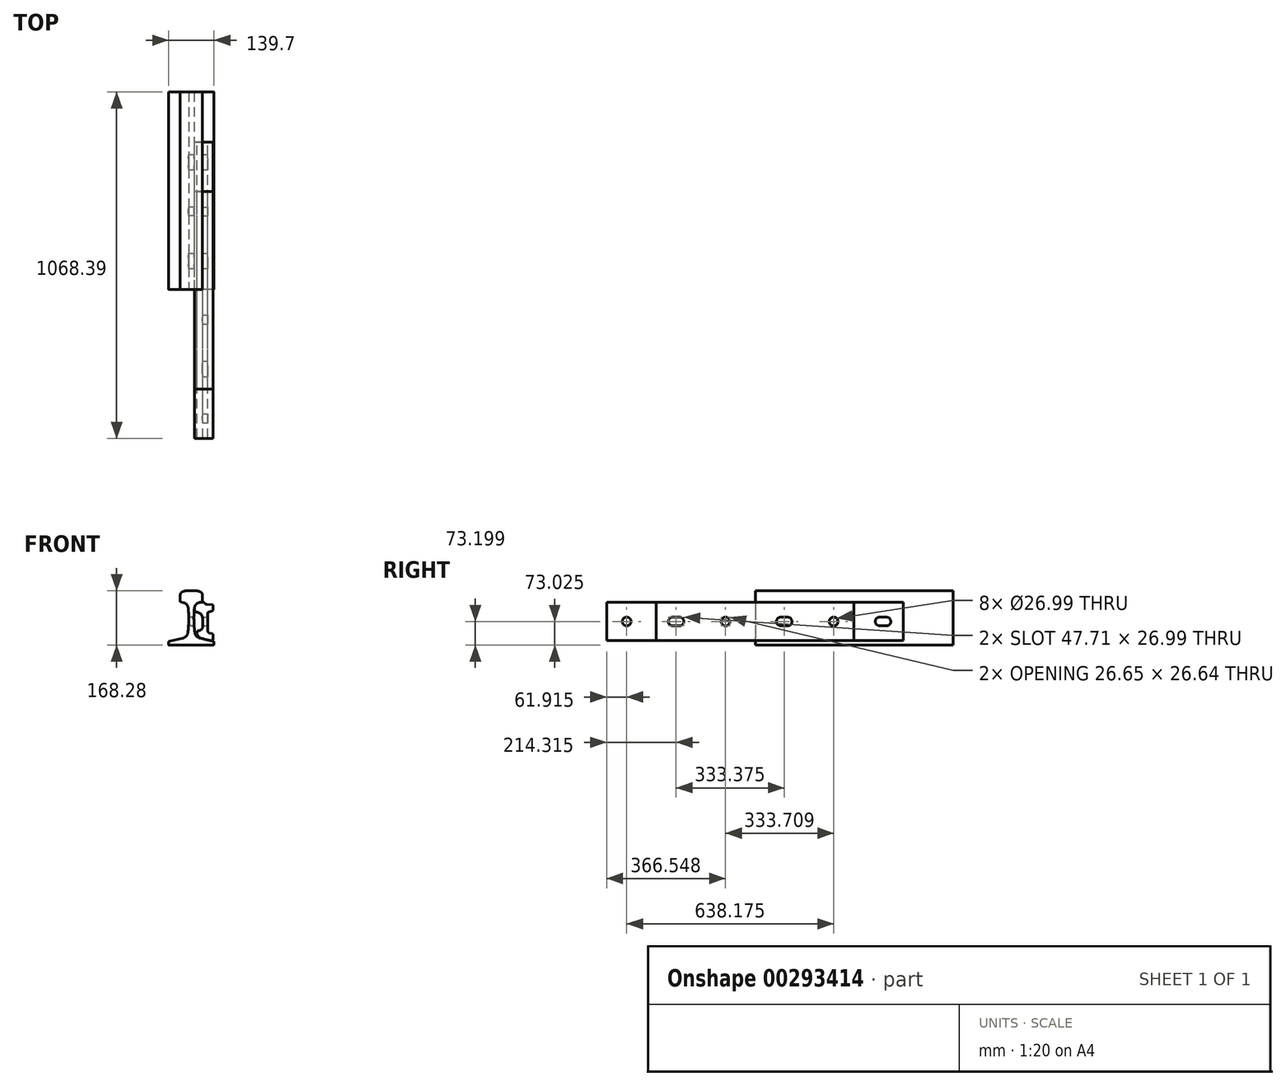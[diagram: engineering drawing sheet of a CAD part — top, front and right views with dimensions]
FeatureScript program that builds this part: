
annotation { "Feature Type Name" : "Feature", "Feature Type Description" : "" }
export const myFeature = defineFeature(function(context is Context, id is Id, definition is map)
    precondition{}
    {
        {
            var Q0;
            Q0=qCreatedBy(makeId("Front.planeOp"),FACE);
            var sketch = newSketch(context, id + "F0", { "sketchPlane" : qUnion([Q0])});
            skLineSegment(sketch, "E0", {"start": v(0, 0) * mm, "end": v(68.26, 0) * mm});
            skArc(sketch, "E1", {"start": v(68.26, 0) * mm, "mid": v(69.39, 0.46) * mm, "end": v(69.85, 1.59) * mm});
            skLineSegment(sketch, "E2", {"start": v(69.85, 1.59) * mm, "end": v(69.85, 9.92) * mm});
            skArc(sketch, "E3", {"start": v(69.85, 9.92) * mm, "mid": v(69.51, 10.9) * mm, "end": v(68.65, 11.46) * mm});
            skLineSegment(sketch, "E4", {"start": v(68.65, 11.46) * mm, "end": v(24.97, 22.35) * mm});
            skArc(sketch, "E5", {"start": v(10.68, 38.47) * mm, "mid": v(15.33, 28.2) * mm, "end": v(24.97, 22.35) * mm});
            skArc(sketch, "E6", {"start": v(8.85, 107.95) * mm, "mid": v(8.06, 73.17) * mm, "end": v(10.68, 38.47) * mm});
            skArc(sketch, "E7", {"start": v(24.04, 131.42) * mm, "mid": v(14.78, 126) * mm, "end": v(9.93, 116.42) * mm});
            skLineSegment(sketch, "E8", {"start": v(24.04, 131.42) * mm, "end": v(33.2, 133.71) * mm});
            skArc(sketch, "E9", {"start": v(33.2, 133.71) * mm, "mid": v(34.14, 134.33) * mm, "end": v(34.49, 135.4) * mm});
            skLineSegment(sketch, "E10", {"start": v(34.49, 135.4) * mm, "end": v(33.98, 155.6) * mm});
            skArc(sketch, "E11", {"start": v(33.98, 155.6) * mm, "mid": v(33.1, 159.4) * mm, "end": v(30.76, 162.51) * mm});
            skArc(sketch, "E12", {"start": v(30.76, 162.51) * mm, "mid": v(28.6, 164.08) * mm, "end": v(26.2, 165.22) * mm});
            skArc(sketch, "E13", {"start": v(26.2, 165.22) * mm, "mid": v(20.23, 166.93) * mm, "end": v(14.09, 167.79) * mm});
            skArc(sketch, "E14", {"start": v(14.09, 167.79) * mm, "mid": v(7.05, 168.15) * mm, "end": v(0, 168.28) * mm});
            skLineSegment(sketch, "E15.MirrorCS", {"start": v(-69.85, 1.59) * mm, "end": v(-69.85, 9.92) * mm});
            skArc(sketch, "E16.MirrorCS", {"start": v(-30.76, 162.51) * mm, "mid": v(-28.6, 164.08) * mm, "end": v(-26.2, 165.22) * mm});
            skArc(sketch, "E17.MirrorCS", {"start": v(-69.85, 9.92) * mm, "mid": v(-69.51, 10.9) * mm, "end": v(-68.65, 11.46) * mm});
            skArc(sketch, "E18.MirrorCS", {"start": v(-68.26, 0) * mm, "mid": v(-69.39, 0.46) * mm, "end": v(-69.85, 1.59) * mm});
            skLineSegment(sketch, "E19.MirrorCS", {"start": v(-24.04, 131.42) * mm, "end": v(-33.2, 133.71) * mm});
            skArc(sketch, "E20.MirrorCS", {"start": v(-33.98, 155.6) * mm, "mid": v(-33.1, 159.4) * mm, "end": v(-30.76, 162.51) * mm});
            skArc(sketch, "E21.MirrorCS", {"start": v(-33.2, 133.71) * mm, "mid": v(-34.14, 134.33) * mm, "end": v(-34.49, 135.4) * mm});
            skLineSegment(sketch, "E22.MirrorCS", {"start": v(-34.49, 135.4) * mm, "end": v(-33.98, 155.6) * mm});
            skArc(sketch, "E23.MirrorCS", {"start": v(-26.2, 165.22) * mm, "mid": v(-20.23, 166.93) * mm, "end": v(-14.09, 167.79) * mm});
            skArc(sketch, "E24.MirrorCS", {"start": v(-14.09, 167.79) * mm, "mid": v(-7.05, 168.15) * mm, "end": v(0, 168.28) * mm});
            skArc(sketch, "E25.MirrorCS", {"start": v(-24.04, 131.42) * mm, "mid": v(-14.78, 126) * mm, "end": v(-9.93, 116.42) * mm});
            skArc(sketch, "E26.MirrorCS", {"start": v(-8.85, 107.95) * mm, "mid": v(-8.06, 73.17) * mm, "end": v(-10.68, 38.47) * mm});
            skArc(sketch, "E27.MirrorCS", {"start": v(-10.68, 38.47) * mm, "mid": v(-15.33, 28.2) * mm, "end": v(-24.97, 22.35) * mm});
            skLineSegment(sketch, "E28.MirrorCS", {"start": v(0, 0) * mm, "end": v(-68.26, 0) * mm});
            skLineSegment(sketch, "E29.MirrorCS", {"start": v(-68.65, 11.46) * mm, "end": v(-24.97, 22.35) * mm});
            skPoint(sketch, "E30", {"position": v(0, 28.58) * mm});
            skLineSegment(sketch, "E31", {"start": v(0, 28.58) * mm, "end": v(-68.65, 11.46) * mm, "construction": true});
            skLineSegment(sketch, "E32", {"start": v(0, 28.58) * mm, "end": v(-71.74, 28.57) * mm, "construction": true});
            skLineSegment(sketch, "E33", {"start": v(-34.49, 165.52) * mm, "end": v(-34.49, 135.4) * mm, "construction": true});
            skPoint(sketch, "E34", {"position": v(0, 125.41) * mm});
            skLineSegment(sketch, "E35", {"start": v(0, 125.41) * mm, "end": v(-57.8, 125.41) * mm, "construction": true});
            skLineSegment(sketch, "E36", {"start": v(0, 125.41) * mm, "end": v(-54.55, 139.05) * mm, "construction": true});
            skArc(sketch, "E37", {"start": v(9.93, 116.42) * mm, "mid": v(9.27, 112.2) * mm, "end": v(8.85, 107.95) * mm});
            skArc(sketch, "E38.MirrorCS", {"start": v(-9.93, 116.42) * mm, "mid": v(-9.27, 112.2) * mm, "end": v(-8.85, 107.95) * mm});
            skLineSegment(sketch, "E39", {"start": v(-18.26, 73.03) * mm, "end": v(91, 73.03) * mm, "construction": true});
            skSolve(sketch);
        }
        {
            var Q0;
            Q0=qSketchRegion(id+"F0",true);
            extrude(context, id + "F1", {"entities" : qUnion([Q0]), "oppositeDirection" : true, "depth" : 609.6 * mm});
        }
        {
            var Q0;
            Q0=qCreatedBy(makeId("Right.planeOp"),FACE);
            cPlane(context, id + "F2", {"entities" : qUnion([Q0]), "cplaneType" : CPlaneType.OFFSET, "offset" : 76.2 * mm, "width" : 152.4 * mm, "height" : 152.4 * mm});
        }
        {
            var Q0;
            Q0=qCreatedBy(id+"F2.planeOp",FACE);
            var sketch = newSketch(context, id + "F3", { "sketchPlane" : qUnion([Q0])});
            skPoint(sketch, "E40", {"position": v(88.9, 73.02) * mm});
            skPoint(sketch, "E41", {"position": v(241.3, 73.03) * mm});
            skPoint(sketch, "E42", {"position": v(393.7, 73.03) * mm});
            skLineSegment(sketch, "E43", {"start": v(-1.59, 185.63) * mm, "end": v(-1.59, -16.47) * mm, "construction": true});
            skPoint(sketch, "E44.MirrorP", {"position": v(-396.88, 73.02) * mm});
            skPoint(sketch, "E45.MirrorP", {"position": v(-244.48, 73.02) * mm});
            skPoint(sketch, "E46.MirrorP", {"position": v(-92.08, 73.02) * mm});
            skLineSegment(sketch, "E47", {"start": v(-254.84, 73.03) * mm, "end": v(-234.11, 73.03) * mm, "construction": true});
            skArc(sketch, "E48", {"start": v(-254.84, 86.52) * mm, "mid": v(-268.33, 73.03) * mm, "end": v(-254.84, 59.53) * mm});
            skArc(sketch, "E49", {"start": v(-234.11, 86.52) * mm, "mid": v(-220.62, 73.02) * mm, "end": v(-234.11, 59.53) * mm});
            skLineSegment(sketch, "E50", {"start": v(-254.84, 86.52) * mm, "end": v(-234.11, 86.52) * mm});
            skLineSegment(sketch, "E51", {"start": v(-254.84, 59.53) * mm, "end": v(-234.11, 59.53) * mm});
            skLineSegment(sketch, "E52", {"start": v(78.54, 73.03) * mm, "end": v(99.26, 73.03) * mm, "construction": true});
            skArc(sketch, "E53", {"start": v(78.54, 86.52) * mm, "mid": v(65.04, 73.03) * mm, "end": v(78.54, 59.53) * mm});
            skArc(sketch, "E54", {"start": v(99.26, 86.52) * mm, "mid": v(112.76, 73.03) * mm, "end": v(99.26, 59.53) * mm});
            skLineSegment(sketch, "E55", {"start": v(78.54, 86.52) * mm, "end": v(99.26, 86.52) * mm});
            skLineSegment(sketch, "E56", {"start": v(78.54, 59.53) * mm, "end": v(99.26, 59.53) * mm});
            skLineSegment(sketch, "E57", {"start": v(383.34, 73.03) * mm, "end": v(404.06, 73.03) * mm, "construction": true});
            skArc(sketch, "E58", {"start": v(383.34, 86.52) * mm, "mid": v(369.84, 73.03) * mm, "end": v(383.34, 59.53) * mm});
            skArc(sketch, "E59", {"start": v(404.06, 86.52) * mm, "mid": v(417.56, 73.03) * mm, "end": v(404.06, 59.53) * mm});
            skLineSegment(sketch, "E60", {"start": v(383.34, 86.52) * mm, "end": v(404.06, 86.52) * mm});
            skLineSegment(sketch, "E61", {"start": v(383.34, 59.53) * mm, "end": v(404.06, 59.53) * mm});
            skCircle(sketch, "E62", {"center": v(-92.08, 73.02) * mm, "radius": 13.5 * mm});
            skCircle(sketch, "E63", {"center": v(241.3, 73.03) * mm, "radius": 13.5 * mm});
            skCircle(sketch, "E64", {"center": v(-396.88, 73.02) * mm, "radius": 13.5 * mm});
            skSolve(sketch);
        }
        {
            var Q0;
            Q0=makeQuery(id+"F0.imprint","IMPRINT",FACE,{"disambiguationData":[TD([[makeQuery(id+"F0.imprint","IMPRINT",EDGE,{"derivedFrom":sQuery(id+"F0.wireOp",EDGE,"E0")}),1.0]])]});
            extrude(context, id + "F4", {"entities" : qUnion([Q0]), "oppositeDirection" : true, "depth" : 609.6 * mm});
        }
        {
            var Q0;
            Q0=sQuery(id+"F3.wireOp",VERTEX,"E40");
            var Q1;
            Q1=sQuery(id+"F3.wireOp",VERTEX,"E41");
            var Q2;
            Q2=makeQuery(id+"F4.opExtrude","SWEPT_BODY",BODY,{"disambiguationData":[OSD([sQuery(id+"F0.wireOp",EDGE,"E0"),sQuery(id+"F0.wireOp",EDGE,"E1"),sQuery(id+"F0.wireOp",EDGE,"E2"),sQuery(id+"F0.wireOp",EDGE,"E3"),sQuery(id+"F0.wireOp",EDGE,"E4"),sQuery(id+"F0.wireOp",EDGE,"E5"),sQuery(id+"F0.wireOp",EDGE,"E6"),sQuery(id+"F0.wireOp",EDGE,"E7"),sQuery(id+"F0.wireOp",EDGE,"E8"),sQuery(id+"F0.wireOp",EDGE,"E9"),sQuery(id+"F0.wireOp",EDGE,"E10"),sQuery(id+"F0.wireOp",EDGE,"E11"),sQuery(id+"F0.wireOp",EDGE,"E12"),sQuery(id+"F0.wireOp",EDGE,"E13"),sQuery(id+"F0.wireOp",EDGE,"E14"),sQuery(id+"F0.wireOp",EDGE,"E15.MirrorCS"),sQuery(id+"F0.wireOp",EDGE,"E16.MirrorCS"),sQuery(id+"F0.wireOp",EDGE,"E17.MirrorCS"),sQuery(id+"F0.wireOp",EDGE,"E18.MirrorCS"),sQuery(id+"F0.wireOp",EDGE,"E19.MirrorCS"),sQuery(id+"F0.wireOp",EDGE,"E20.MirrorCS"),sQuery(id+"F0.wireOp",EDGE,"E21.MirrorCS"),sQuery(id+"F0.wireOp",EDGE,"E22.MirrorCS"),sQuery(id+"F0.wireOp",EDGE,"E23.MirrorCS"),sQuery(id+"F0.wireOp",EDGE,"E24.MirrorCS"),sQuery(id+"F0.wireOp",EDGE,"E25.MirrorCS"),sQuery(id+"F0.wireOp",EDGE,"E26.MirrorCS"),sQuery(id+"F0.wireOp",EDGE,"E27.MirrorCS"),sQuery(id+"F0.wireOp",EDGE,"E28.MirrorCS"),sQuery(id+"F0.wireOp",EDGE,"E29.MirrorCS"),sQuery(id+"F0.wireOp",EDGE,"E37"),sQuery(id+"F0.wireOp",EDGE,"E38.MirrorCS")])]});
            hole(context, id + "F5", {"style" : HoleStyle.SIMPLE, "endStyle" : HoleEndStyle.THROUGH, "holeDiameter" : 26.99 * mm, "startFromSketch" : true, "locations" : qUnion([Q0, Q1]), "scope" : qUnion([Q2]), "isTappedThrough" : true});
        }
        {
            var Q0;
            Q0=makeQuery(id+"F0.imprint","IMPRINT",FACE,{"disambiguationData":[TD([[makeQuery(id+"F0.imprint","IMPRINT",EDGE,{"derivedFrom":sQuery(id+"F0.wireOp",EDGE,"E0")}),1.0]])]});
            extrude(context, id + "F6", {"entities" : qUnion([Q0]), "oppositeDirection" : true, "depth" : 609.6 * mm});
        }
        {
            var Q0;
            Q0=sQuery(id+"F3.wireOp",VERTEX,"E40");
            var Q1;
            Q1=sQuery(id+"F3.wireOp",VERTEX,"E41");
            var Q2;
            Q2=sQuery(id+"F3.wireOp",VERTEX,"E42");
            var Q3;
            Q3=makeQuery(id+"F6.opExtrude","SWEPT_BODY",BODY,{"disambiguationData":[OSD([sQuery(id+"F0.wireOp",EDGE,"E0"),sQuery(id+"F0.wireOp",EDGE,"E1"),sQuery(id+"F0.wireOp",EDGE,"E2"),sQuery(id+"F0.wireOp",EDGE,"E3"),sQuery(id+"F0.wireOp",EDGE,"E4"),sQuery(id+"F0.wireOp",EDGE,"E5"),sQuery(id+"F0.wireOp",EDGE,"E6"),sQuery(id+"F0.wireOp",EDGE,"E7"),sQuery(id+"F0.wireOp",EDGE,"E8"),sQuery(id+"F0.wireOp",EDGE,"E9"),sQuery(id+"F0.wireOp",EDGE,"E10"),sQuery(id+"F0.wireOp",EDGE,"E11"),sQuery(id+"F0.wireOp",EDGE,"E12"),sQuery(id+"F0.wireOp",EDGE,"E13"),sQuery(id+"F0.wireOp",EDGE,"E14"),sQuery(id+"F0.wireOp",EDGE,"E15.MirrorCS"),sQuery(id+"F0.wireOp",EDGE,"E16.MirrorCS"),sQuery(id+"F0.wireOp",EDGE,"E17.MirrorCS"),sQuery(id+"F0.wireOp",EDGE,"E18.MirrorCS"),sQuery(id+"F0.wireOp",EDGE,"E19.MirrorCS"),sQuery(id+"F0.wireOp",EDGE,"E20.MirrorCS"),sQuery(id+"F0.wireOp",EDGE,"E21.MirrorCS"),sQuery(id+"F0.wireOp",EDGE,"E22.MirrorCS"),sQuery(id+"F0.wireOp",EDGE,"E23.MirrorCS"),sQuery(id+"F0.wireOp",EDGE,"E24.MirrorCS"),sQuery(id+"F0.wireOp",EDGE,"E25.MirrorCS"),sQuery(id+"F0.wireOp",EDGE,"E26.MirrorCS"),sQuery(id+"F0.wireOp",EDGE,"E27.MirrorCS"),sQuery(id+"F0.wireOp",EDGE,"E28.MirrorCS"),sQuery(id+"F0.wireOp",EDGE,"E29.MirrorCS"),sQuery(id+"F0.wireOp",EDGE,"E37"),sQuery(id+"F0.wireOp",EDGE,"E38.MirrorCS")])]});
            hole(context, id + "F7", {"style" : HoleStyle.SIMPLE, "endStyle" : HoleEndStyle.THROUGH, "holeDiameter" : 26.99 * mm, "startFromSketch" : true, "locations" : qUnion([Q0, Q1, Q2]), "scope" : qUnion([Q3]), "isTappedThrough" : true});
        }
        {
            var Q0;
            Q0=qCreatedBy(makeId("Front.planeOp"),FACE);
            cPlane(context, id + "F8", {"entities" : qUnion([Q0]), "cplaneType" : CPlaneType.OFFSET, "offset" : 1.59 * mm, "width" : 152.4 * mm, "height" : 152.4 * mm});
        }
        {
            var Q0;
            Q0=qCreatedBy(id+"F8.planeOp",FACE);
            var sketch = newSketch(context, id + "F9", { "sketchPlane" : qUnion([Q0])});
            skArc(sketch, "E65", {"start": v(30.39, 21.08) * mm, "mid": v(46.46, 16.84) * mm, "end": v(62.8, 13.78) * mm});
            skArc(sketch, "E66", {"start": v(62.8, 13.78) * mm, "mid": v(65.35, 14.51) * mm, "end": v(66.45, 16.92) * mm});
            skLineSegment(sketch, "E67", {"start": v(66.45, 16.92) * mm, "end": v(66.45, 32.53) * mm});
            skArc(sketch, "E68", {"start": v(66.45, 32.53) * mm, "mid": v(65.78, 34.48) * mm, "end": v(64.04, 35.6) * mm});
            skLineSegment(sketch, "E69", {"start": v(64.04, 35.6) * mm, "end": v(55.61, 37.72) * mm});
            skArc(sketch, "E70", {"start": v(50.8, 43.88) * mm, "mid": v(52.15, 39.97) * mm, "end": v(55.61, 37.72) * mm});
            skLineSegment(sketch, "E71", {"start": v(50.8, 43.88) * mm, "end": v(50.8, 98.74) * mm});
            skArc(sketch, "E72", {"start": v(52.9, 101.73) * mm, "mid": v(51.38, 100.57) * mm, "end": v(50.8, 98.74) * mm});
            skLineSegment(sketch, "E73", {"start": v(52.9, 101.73) * mm, "end": v(64.58, 105.96) * mm});
            skArc(sketch, "E74", {"start": v(64.58, 105.96) * mm, "mid": v(66.1, 107.12) * mm, "end": v(66.67, 108.94) * mm});
            skLineSegment(sketch, "E75", {"start": v(66.67, 108.94) * mm, "end": v(66.67, 121.63) * mm});
            skArc(sketch, "E76", {"start": v(66.67, 121.63) * mm, "mid": v(65.82, 123.8) * mm, "end": v(63.72, 124.8) * mm});
            skLineSegment(sketch, "E77", {"start": v(63.72, 124.8) * mm, "end": v(47.9, 125.93) * mm});
            skArc(sketch, "E78", {"start": v(41.15, 129.52) * mm, "mid": v(44.14, 127.01) * mm, "end": v(47.9, 125.93) * mm});
            skArc(sketch, "E79", {"start": v(41.15, 129.52) * mm, "mid": v(37.58, 132.22) * mm, "end": v(33.13, 132.78) * mm});
            skLineSegment(sketch, "E80", {"start": v(33.13, 132.78) * mm, "end": v(26.34, 131.87) * mm});
            skArc(sketch, "E81", {"start": v(26.34, 131.87) * mm, "mid": v(12.73, 123.07) * mm, "end": v(10.81, 106.98) * mm});
            skArc(sketch, "E82", {"start": v(10.81, 106.98) * mm, "mid": v(13.26, 103.4) * mm, "end": v(17.24, 101.67) * mm});
            skArc(sketch, "E83", {"start": v(34.92, 81.5) * mm, "mid": v(29.88, 94.9) * mm, "end": v(17.24, 101.67) * mm});
            skLineSegment(sketch, "E84", {"start": v(34.92, 81.5) * mm, "end": v(34.92, 57.4) * mm});
            skArc(sketch, "E85", {"start": v(22.61, 44.86) * mm, "mid": v(31.33, 48.62) * mm, "end": v(34.92, 57.4) * mm});
            skArc(sketch, "E86", {"start": v(22.61, 44.86) * mm, "mid": v(18.57, 43.11) * mm, "end": v(16.93, 39.03) * mm});
            skArc(sketch, "E87", {"start": v(16.93, 39.03) * mm, "mid": v(20.72, 27.84) * mm, "end": v(30.39, 21.08) * mm});
            skSolve(sketch);
        }
        {
            var Q0;
            Q0=makeQuery(id+"F9.imprint","IMPRINT",FACE,{"disambiguationData":[TD([[makeQuery(id+"F9.imprint","IMPRINT",EDGE,{"derivedFrom":sQuery(id+"F9.wireOp",EDGE,"E65")}),1.0]])]});
            extrude(context, id + "F10", {"entities" : qUnion([Q0]), "depth" : 609.6 * mm, "symmetric" : true});
        }
        {
            var Q0;
            Q0=makeQuery(id+"F3.imprint","IMPRINT",FACE,{"disambiguationData":[TD([[makeQuery(id+"F3.imprint","IMPRINT",EDGE,{"derivedFrom":sQuery(id+"F3.wireOp",EDGE,"E48")}),1.0]])]});
            var Q1;
            Q1=makeQuery(id+"F3.imprint","IMPRINT",FACE,{"disambiguationData":[TD([[makeQuery(id+"F3.imprint","IMPRINT",EDGE,{"derivedFrom":sQuery(id+"F3.wireOp",EDGE,"E62")}),1.0]])]});
            var Q2;
            Q2=makeQuery(id+"F3.imprint","IMPRINT",FACE,{"disambiguationData":[TD([[makeQuery(id+"F3.imprint","IMPRINT",EDGE,{"derivedFrom":sQuery(id+"F3.wireOp",EDGE,"E53")}),1.0]])]});
            var Q3;
            Q3=makeQuery(id+"F3.imprint","IMPRINT",FACE,{"disambiguationData":[TD([[makeQuery(id+"F3.imprint","IMPRINT",EDGE,{"derivedFrom":sQuery(id+"F3.wireOp",EDGE,"E63")}),1.0]])]});
            extrude(context, id + "F11", {"entities" : qUnion([Q0, Q1, Q2, Q3]), "operationType" : NewBodyOperationType.REMOVE, "endBound" : BoundingType.THROUGH_ALL, "oppositeDirection" : true, "depth" : 25.4 * mm});
        }
        {
            var Q0;
            Q0=makeQuery(id+"F9.imprint","IMPRINT",FACE,{"disambiguationData":[TD([[makeQuery(id+"F9.imprint","IMPRINT",EDGE,{"derivedFrom":sQuery(id+"F9.wireOp",EDGE,"E65")}),1.0]])]});
            extrude(context, id + "F12", {"entities" : qUnion([Q0]), "depth" : 914.4 * mm, "symmetric" : true});
        }
        {
            var Q0;
            Q0=makeQuery(id+"F3.imprint","IMPRINT",FACE,{"disambiguationData":[TD([[makeQuery(id+"F3.imprint","IMPRINT",EDGE,{"derivedFrom":sQuery(id+"F3.wireOp",EDGE,"E64")}),1.0]])]});
            var Q1;
            Q1=makeQuery(id+"F3.imprint","IMPRINT",FACE,{"disambiguationData":[TD([[makeQuery(id+"F3.imprint","IMPRINT",EDGE,{"derivedFrom":sQuery(id+"F3.wireOp",EDGE,"E48")}),1.0]])]});
            var Q2;
            Q2=makeQuery(id+"F3.imprint","IMPRINT",FACE,{"disambiguationData":[TD([[makeQuery(id+"F3.imprint","IMPRINT",EDGE,{"derivedFrom":sQuery(id+"F3.wireOp",EDGE,"E62")}),1.0]])]});
            var Q3;
            Q3=makeQuery(id+"F3.imprint","IMPRINT",FACE,{"disambiguationData":[TD([[makeQuery(id+"F3.imprint","IMPRINT",EDGE,{"derivedFrom":sQuery(id+"F3.wireOp",EDGE,"E53")}),1.0]])]});
            var Q4;
            Q4=makeQuery(id+"F3.imprint","IMPRINT",FACE,{"disambiguationData":[TD([[makeQuery(id+"F3.imprint","IMPRINT",EDGE,{"derivedFrom":sQuery(id+"F3.wireOp",EDGE,"E63")}),1.0]])]});
            var Q5;
            Q5=makeQuery(id+"F3.imprint","IMPRINT",FACE,{"disambiguationData":[TD([[makeQuery(id+"F3.imprint","IMPRINT",EDGE,{"derivedFrom":sQuery(id+"F3.wireOp",EDGE,"E58")}),1.0]])]});
            extrude(context, id + "F13", {"entities" : qUnion([Q0, Q1, Q2, Q3, Q4, Q5]), "operationType" : NewBodyOperationType.REMOVE, "endBound" : BoundingType.THROUGH_ALL, "oppositeDirection" : true, "depth" : 25.4 * mm});
        }
    });
